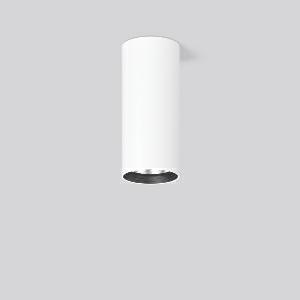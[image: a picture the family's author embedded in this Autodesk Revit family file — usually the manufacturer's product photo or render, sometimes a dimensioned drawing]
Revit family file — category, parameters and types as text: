
# Revit family: heledon_mini_a_931208_002_fb68
name_source: partatom
category: Lighting Fixtures
units: mm (PartAtom-declared; Revit-internal decimal feet)

## family parameters
Cut with Voids When Loaded = No
Host = Face
Light Source = No
Part Type = Normal
Room Calculation Point = No
Round Connector Dimension = Use Diameter
Shared = No

## types (1)
- HELEDON mini A (1 x LED Modul 930, 3550 lm, 3000)
    Apparent Load = 29 VA
    Approval mark = CE
    CIE Flux Codes = 100 100 100 100 100
    Color Rendering = 90
    Color Temperature = 3000
    Default Elevation = 1800 mm
    Description = Series: HELEDON mini
Cylindrical surface-mounted downlight. Housing: die-cast aluminium, powder-coated. Internal ceiling frame polycarbonate with bayonet mounting. Black plastic ring and recessed LED to prevent glare from the side. Optical assembly with reflector made of MIRO-Silver with 98% total light reflection for outstanding efficiency - can be changed without tools. Best colour rendering index Ra>90. Suitable for Ceiling mounting. Easy installation with a separate ceiling frame with bayonet mounting and plug connection. Driver integrated. Connected via plug-in connector. High quality converter without flickering and stroboscopic effect. The following accessories can be mounted without use of tools: interchangeable lenses, decorative glasses, honeycomb louvre, clear and frosted diffusers, white interchangeable plastic ring. 
Colour: traffic white, matt (RAL 9016)
Diameter: 87 mm
Height: 197 mm
Lamp: LED
Socket: without socket
Colour temperature: 3000K
Colour rendering index (CRI): 92
System power: 29 W
Rated luminous flux: 3550 lm
Luminous efficiency: 122 lm/W
Control gear: Regulated power supply
Protection class: I
Type of protection: IP 20
    Height = 197 mm
    Lamp = 1 x LED Modul 930
    Lamp Light Flux = 3550 lm
    Lamp count = 1
    Length = 87 mm
    Lifetime = 50000 h
    Luminous efficacy = 122 lm/W
    Manufacturer = RZB
    ModVariant = No
    Model = 931208.002
    Mounting Place = Ceiling
    Mounting Type = Surface mounted
    Number of Poles = 1
    OnlyDefault = Yes
    Power Factor = 1
    Product Name = HELEDON mini A
    Product group = Surface mounted downlights
    ProductGroupID = 302
    Protection Class = Protection class I
    Protection Degree = IP 20
    RLX_Detail_Level = 1
    RLX_Emergency_Light_Flux = 0 lm
    RLX_Emergency_Type = 0
    RLX_Emergency_Type_DB = No
    RlxData = <blob elided: 106857 chars, md5=85590d2d>
    Socket = socket
    Standby Power = 0 W
    System Light Flux = 3550 lm
    System Power = 29 W
    Type Comments = Product without accessories
    Type Image = 931188.002.jpg
    URL = http://relux.com
    VarID = ---
    Voltage = 230 V
    Voltage Range = 220-240 V
    Weight = 0.00 kg
    Width = 0 mm  [stored 0 ft]

note: [stored X ft] marks values corroborated as IEEE doubles in the binary element streams (Revit-internal decimal feet)

## geometry (parser evidence)
native form markers: Blend x4, Sweep x8
no freeform markers — native parametric forms only
